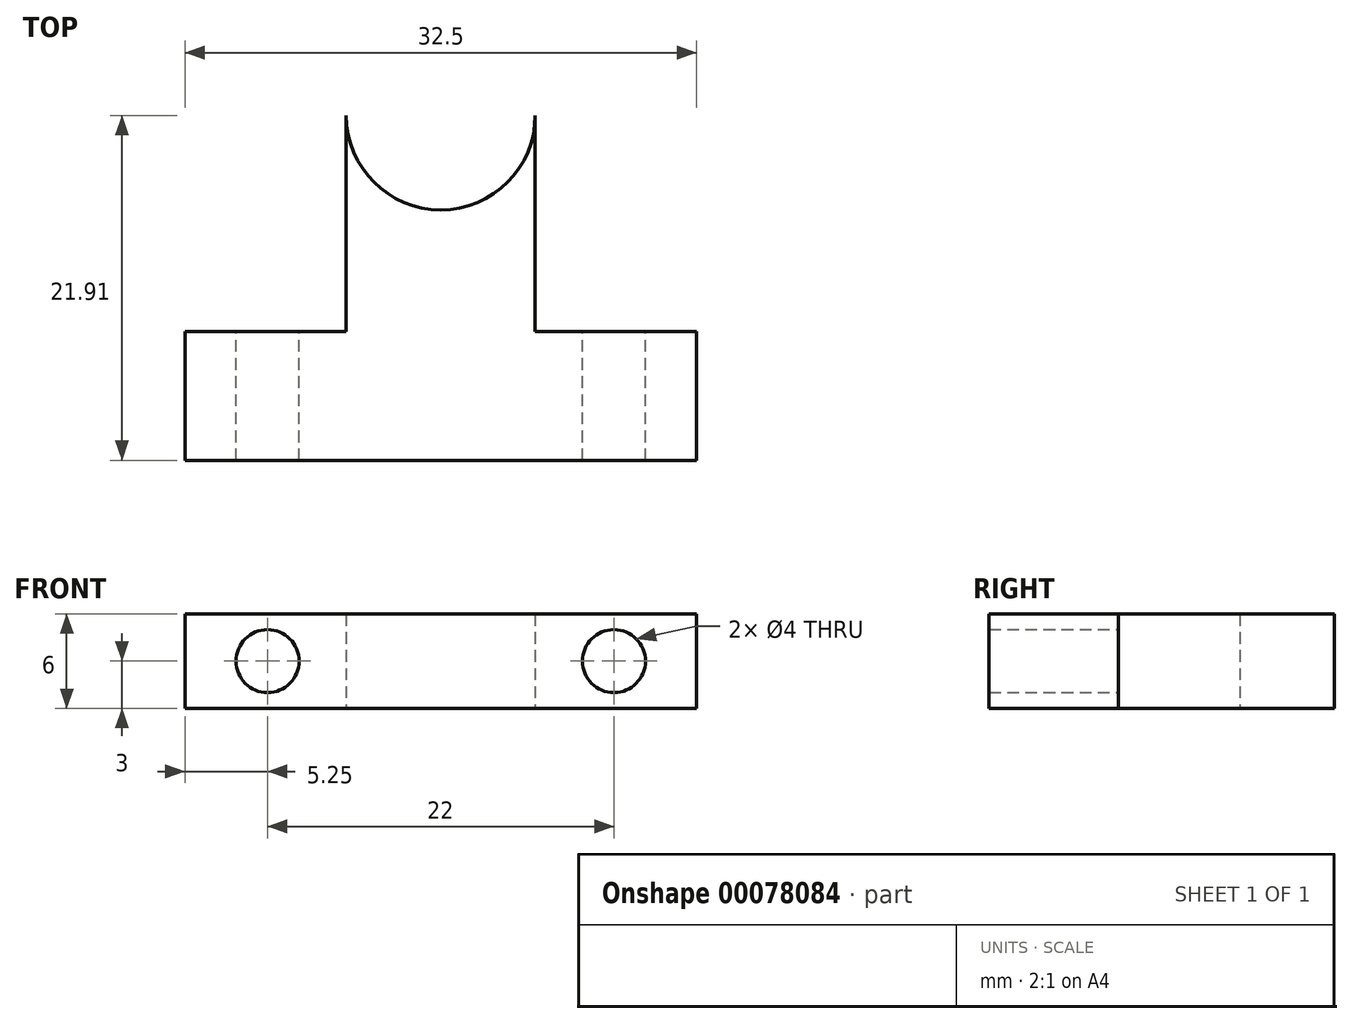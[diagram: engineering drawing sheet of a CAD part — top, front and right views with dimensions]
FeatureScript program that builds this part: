
annotation { "Feature Type Name" : "Feature", "Feature Type Description" : "" }
export const myFeature = defineFeature(function(context is Context, id is Id, definition is map)
    precondition{}
    {
        {
            var Q0;
            Q0=qCreatedBy(makeId("Top.planeOp"),FACE);
            var sketch = newSketch(context, id + "F0", { "sketchPlane" : qUnion([Q0])});
            skLineSegment(sketch, "E0", {"start": v(6, 0) * mm, "end": v(6, 13.71) * mm});
            skLineSegment(sketch, "E1", {"start": v(6, 13.71) * mm, "end": v(-6, 13.71) * mm, "construction": true});
            skLineSegment(sketch, "E2", {"start": v(-6, 13.71) * mm, "end": v(-6, 0) * mm});
            skArc(sketch, "E3", {"start": v(-6, 13.71) * mm, "mid": v(0, 7.71) * mm, "end": v(6, 13.71) * mm});
            skLineSegment(sketch, "E4", {"start": v(-6, 0) * mm, "end": v(-16.25, 0) * mm});
            skLineSegment(sketch, "E5", {"start": v(-16.25, 0) * mm, "end": v(-16.25, -8.2) * mm});
            skLineSegment(sketch, "E6", {"start": v(6, 0) * mm, "end": v(16.25, 0) * mm});
            skLineSegment(sketch, "E7", {"start": v(16.25, 0) * mm, "end": v(16.25, -8.2) * mm});
            skLineSegment(sketch, "E8", {"start": v(16.25, -8.2) * mm, "end": v(-16.25, -8.2) * mm});
            skSolve(sketch);
        }
        {
            var Q0;
            Q0 = qSketchRegion(id + "F0", true);
            extrude(context, id + "F1", {"entities" : qUnion([Q0]), "depth" : 6 * mm});
        }
        {
            var Q0;
            Q0=makeQuery(id+"F1.opExtrude","SWEPT_FACE",FACE,{"disambiguationData":[OSD([sQuery(id+"F0.wireOp",EDGE,"E8")])]});
            var sketch = newSketch(context, id + "F2", { "sketchPlane" : qUnion([Q0])});
            skPoint(sketch, "E9", {"position": v(-11, 3) * mm});
            skPoint(sketch, "E10.MirrorP", {"position": v(11, 3) * mm});
            skSolve(sketch);
        }
        {
            var Q0;
            Q0=sQuery(id+"F2.wireOp",VERTEX,"E9");
            var Q1;
            Q1=sQuery(id+"F2.wireOp",VERTEX,"E10.MirrorP");
            var Q2;
            Q2=makeQuery(id+"F1.opExtrude","SWEPT_BODY",BODY,{"disambiguationData":[OSD([sQuery(id+"F0.wireOp",EDGE,"E0"),sQuery(id+"F0.wireOp",EDGE,"E2"),sQuery(id+"F0.wireOp",EDGE,"E3"),sQuery(id+"F0.wireOp",EDGE,"E4"),sQuery(id+"F0.wireOp",EDGE,"E5"),sQuery(id+"F0.wireOp",EDGE,"E6"),sQuery(id+"F0.wireOp",EDGE,"E7"),sQuery(id+"F0.wireOp",EDGE,"E8")])]});
            hole(context, id + "F3", {"style" : HoleStyle.SIMPLE, "endStyle" : HoleEndStyle.THROUGH, "holeDiameter" : 4 * mm, "locations" : qUnion([Q0, Q1]), "scope" : qUnion([Q2]), "isTappedThrough" : true});
        }
    });
